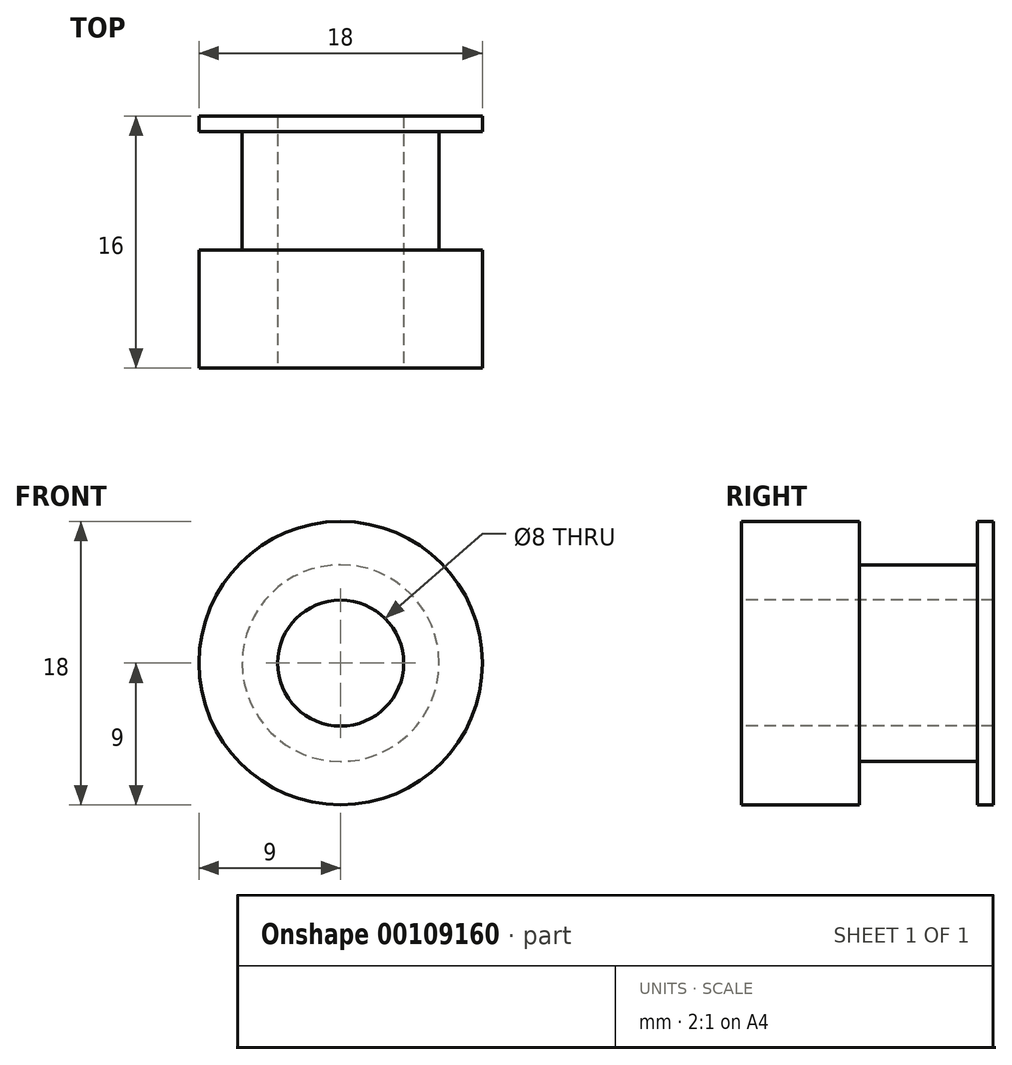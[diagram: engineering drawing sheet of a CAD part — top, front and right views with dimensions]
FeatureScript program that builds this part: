
annotation { "Feature Type Name" : "Feature", "Feature Type Description" : "" }
export const myFeature = defineFeature(function(context is Context, id is Id, definition is map)
    precondition{}
    {
        {
            var Q0;
            Q0=qCreatedBy(makeId("Right.planeOp"),FACE);
            var sketch = newSketch(context, id + "F0", { "sketchPlane" : qUnion([Q0])});
            skLineSegment(sketch, "E0", {"start": v(0, 0) * mm, "end": v(16, 0) * mm, "construction": true});
            skLineSegment(sketch, "E1", {"start": v(16, 0) * mm, "end": v(16, 4) * mm, "construction": true});
            skLineSegment(sketch, "E2", {"start": v(16, 4) * mm, "end": v(0, 4) * mm});
            skLineSegment(sketch, "E3", {"start": v(0, 4) * mm, "end": v(0, 9) * mm});
            skLineSegment(sketch, "E4", {"start": v(0, 9) * mm, "end": v(7.5, 9) * mm});
            skLineSegment(sketch, "E5", {"start": v(7.5, 9) * mm, "end": v(7.5, 6.25) * mm});
            skLineSegment(sketch, "E6", {"start": v(7.5, 6.25) * mm, "end": v(15, 6.25) * mm});
            skLineSegment(sketch, "E7", {"start": v(15, 6.25) * mm, "end": v(15, 9) * mm});
            skLineSegment(sketch, "E8", {"start": v(15, 9) * mm, "end": v(16, 9) * mm});
            skLineSegment(sketch, "E9", {"start": v(16, 9) * mm, "end": v(16, 4) * mm});
            skSolve(sketch);
        }
        {
            var Q0;
            Q0=qSketchRegion(id+"F0",true);
            var Q1;
            Q1=sQuery(id+"F0.wireOp",EDGE,"E0");
            revolve(context, id + "F1", {"entities" : qUnion([Q0]), "axis" : qUnion([Q1]), "revolveType" : RevolveType.FULL});
        }
    });
